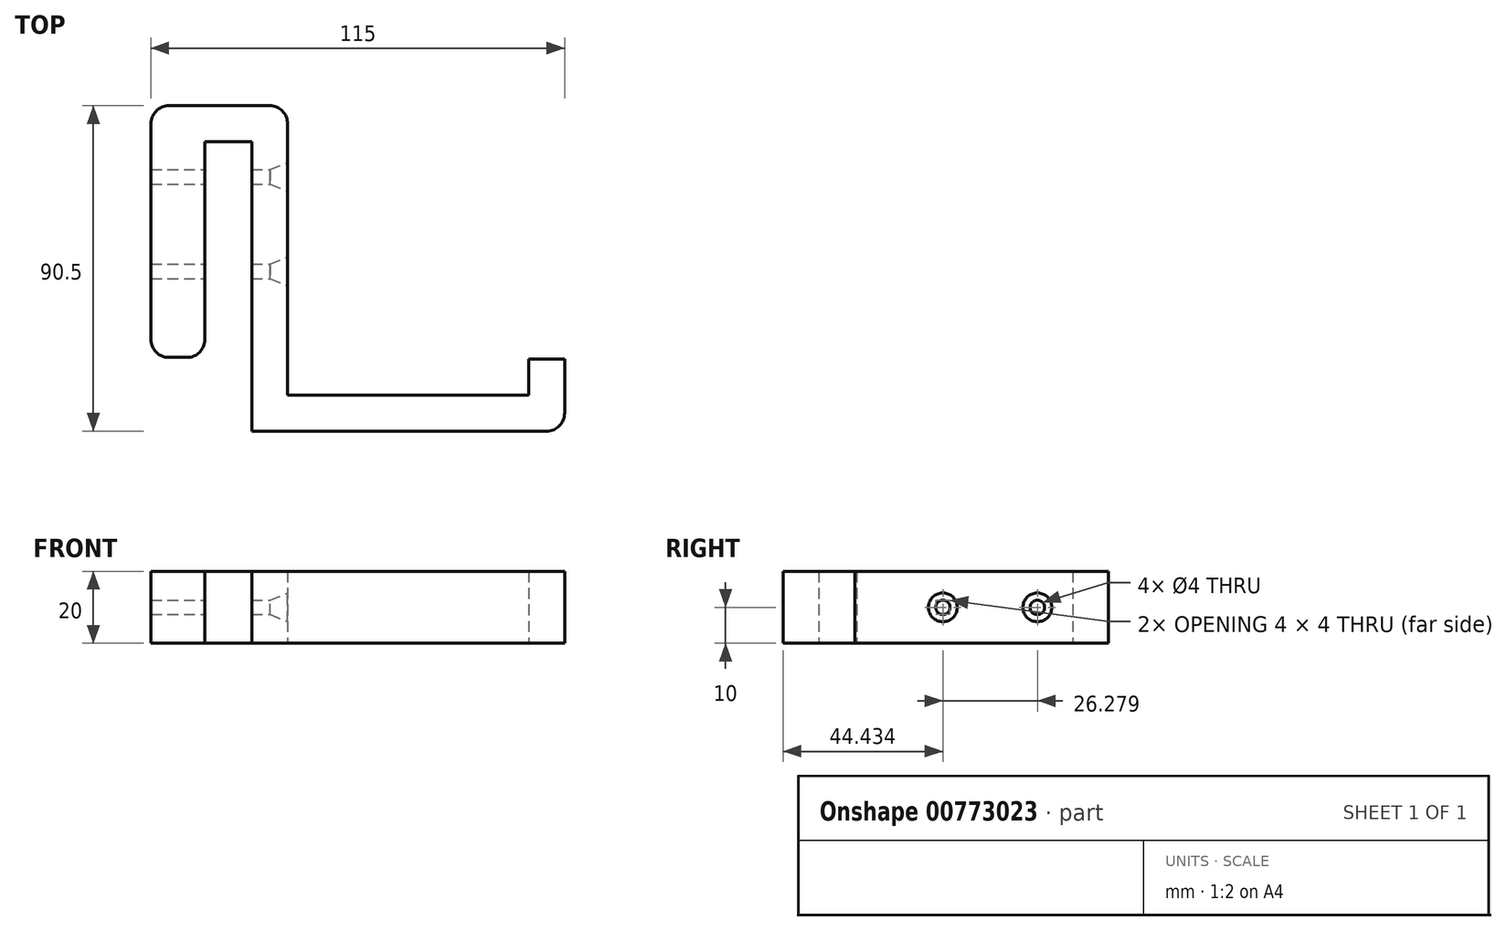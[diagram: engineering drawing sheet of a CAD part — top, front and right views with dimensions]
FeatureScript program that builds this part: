
annotation { "Feature Type Name" : "Feature", "Feature Type Description" : "" }
export const myFeature = defineFeature(function(context is Context, id is Id, definition is map)
    precondition{}
    {
        {
            var Q0;
            Q0=qCreatedBy(makeId("Top.planeOp"),FACE);
            var sketch = newSketch(context, id + "F0", { "sketchPlane" : qUnion([Q0])});
            skLineSegment(sketch, "E0", {"start": v(0, 0) * mm, "end": v(0, 80.5) * mm});
            skLineSegment(sketch, "E1", {"start": v(0, 80.5) * mm, "end": v(-13, 80.5) * mm});
            skLineSegment(sketch, "E2", {"start": v(-13, 80.5) * mm, "end": v(-13, 20.5) * mm});
            skLineSegment(sketch, "E3", {"start": v(0, 0) * mm, "end": v(87, 0) * mm});
            skLineSegment(sketch, "E4", {"start": v(87, 0) * mm, "end": v(87, 20) * mm});
            skLineSegment(sketch, "E5", {"start": v(-13, 20.5) * mm, "end": v(-28, 20.5) * mm});
            skLineSegment(sketch, "E6", {"start": v(-28, 20.5) * mm, "end": v(-28, 90.5) * mm});
            skLineSegment(sketch, "E7", {"start": v(-28, 90.5) * mm, "end": v(10, 90.5) * mm});
            skLineSegment(sketch, "E8", {"start": v(10, 90.5) * mm, "end": v(10, 10) * mm});
            skLineSegment(sketch, "E9", {"start": v(10, 10) * mm, "end": v(77, 10) * mm});
            skLineSegment(sketch, "E10", {"start": v(77, 10) * mm, "end": v(77, 20) * mm});
            skLineSegment(sketch, "E11", {"start": v(77, 20) * mm, "end": v(87, 20) * mm});
            skSolve(sketch);
        }
        {
            var Q0;
            Q0=makeQuery(id+"F0.imprint","IMPRINT",FACE,{"disambiguationData":[TD([[makeQuery(id+"F0.imprint","IMPRINT",EDGE,{"derivedFrom":sQuery(id+"F0.wireOp",EDGE,"E0")}),-1.0]])]});
            extrude(context, id + "F1", {"entities" : qUnion([Q0]), "depth" : 20 * mm, "offsetDistance" : 25 * mm});
        }
        {
            var Q0;
            Q0=makeQuery(id+"F1.opExtrude","SWEPT_EDGE",EDGE,{"disambiguationData":[OSD([sQuery(id+"F0.wireOp",EDGE,"E3"),sQuery(id+"F0.wireOp",EDGE,"E4")])]});
            fillet(context, id + "F2", {"entities" : qUnion([Q0]), "radius" : 5 * mm, "tangentPropagation" : true, "allowEdgeOverflow" : false});
        }
        {
            var Q0;
            Q0=makeQuery(id+"F1.opExtrude","SWEPT_EDGE",EDGE,{"disambiguationData":[OSD([sQuery(id+"F0.wireOp",EDGE,"E2"),sQuery(id+"F0.wireOp",EDGE,"E5")])]});
            var Q1;
            Q1=makeQuery(id+"F1.opExtrude","SWEPT_EDGE",EDGE,{"disambiguationData":[OSD([sQuery(id+"F0.wireOp",EDGE,"E5"),sQuery(id+"F0.wireOp",EDGE,"E6")])]});
            fillet(context, id + "F3", {"entities" : qUnion([Q0, Q1]), "radius" : 5 * mm, "tangentPropagation" : true, "allowEdgeOverflow" : false});
        }
        {
            var Q0;
            Q0=makeQuery(id+"F1.opExtrude","SWEPT_EDGE",EDGE,{"disambiguationData":[OSD([sQuery(id+"F0.wireOp",EDGE,"E6"),sQuery(id+"F0.wireOp",EDGE,"E7")])]});
            var Q1;
            Q1=makeQuery(id+"F1.opExtrude","SWEPT_EDGE",EDGE,{"disambiguationData":[OSD([sQuery(id+"F0.wireOp",EDGE,"E7"),sQuery(id+"F0.wireOp",EDGE,"E8")])]});
            fillet(context, id + "F4", {"entities" : qUnion([Q0, Q1]), "radius" : 5 * mm, "tangentPropagation" : true, "allowEdgeOverflow" : false});
        }
        {
            var Q0;
            Q0=makeQuery(id+"F1.opExtrude","SWEPT_FACE",FACE,{"disambiguationData":[OSD([sQuery(id+"F0.wireOp",EDGE,"E8")])]});
            var sketch = newSketch(context, id + "F5", { "sketchPlane" : qUnion([Q0])});
            skLineSegment(sketch, "E12", {"start": v(85.5, 10) * mm, "end": v(10, 10) * mm, "construction": true});
            skLineSegment(sketch, "E13", {"start": v(70.71, 20) * mm, "end": v(70.71, 0) * mm, "construction": true});
            skLineSegment(sketch, "E14", {"start": v(44.43, 20) * mm, "end": v(44.43, 0) * mm, "construction": true});
            skPoint(sketch, "E15", {"position": v(70.71, 10) * mm});
            skPoint(sketch, "E16", {"position": v(44.43, 10) * mm});
            skSolve(sketch);
        }
        {
            var Q0;
            Q0=sQuery(id+"F5.wireOp",VERTEX,"E15");
            var Q1;
            Q1=sQuery(id+"F5.wireOp",VERTEX,"E16");
            var Q2;
            Q2=makeQuery(id+"F1.opExtrude","SWEPT_BODY",BODY,{"disambiguationData":[OSD([sQuery(id+"F0.wireOp",EDGE,"E0"),sQuery(id+"F0.wireOp",EDGE,"E1"),sQuery(id+"F0.wireOp",EDGE,"E2"),sQuery(id+"F0.wireOp",EDGE,"E3"),sQuery(id+"F0.wireOp",EDGE,"E4"),sQuery(id+"F0.wireOp",EDGE,"E5"),sQuery(id+"F0.wireOp",EDGE,"E6"),sQuery(id+"F0.wireOp",EDGE,"E7"),sQuery(id+"F0.wireOp",EDGE,"E8"),sQuery(id+"F0.wireOp",EDGE,"E9"),sQuery(id+"F0.wireOp",EDGE,"E10"),sQuery(id+"F0.wireOp",EDGE,"E11")])]});
            hole(context, id + "F6", {"style" : HoleStyle.C_SINK, "endStyle" : HoleEndStyle.THROUGH, "holeDiameter" : 4 * mm, "cSinkDiameter" : 8 * mm, "cSinkAngle" : 45 * degree, "majorDiameter" : 5 * mm, "isTappedThrough" : true, "tappedDepth" : 12 * mm, "tapClearance" : 3, "locations" : qUnion([Q0, Q1]), "scope" : qUnion([Q2])});
        }
    });
